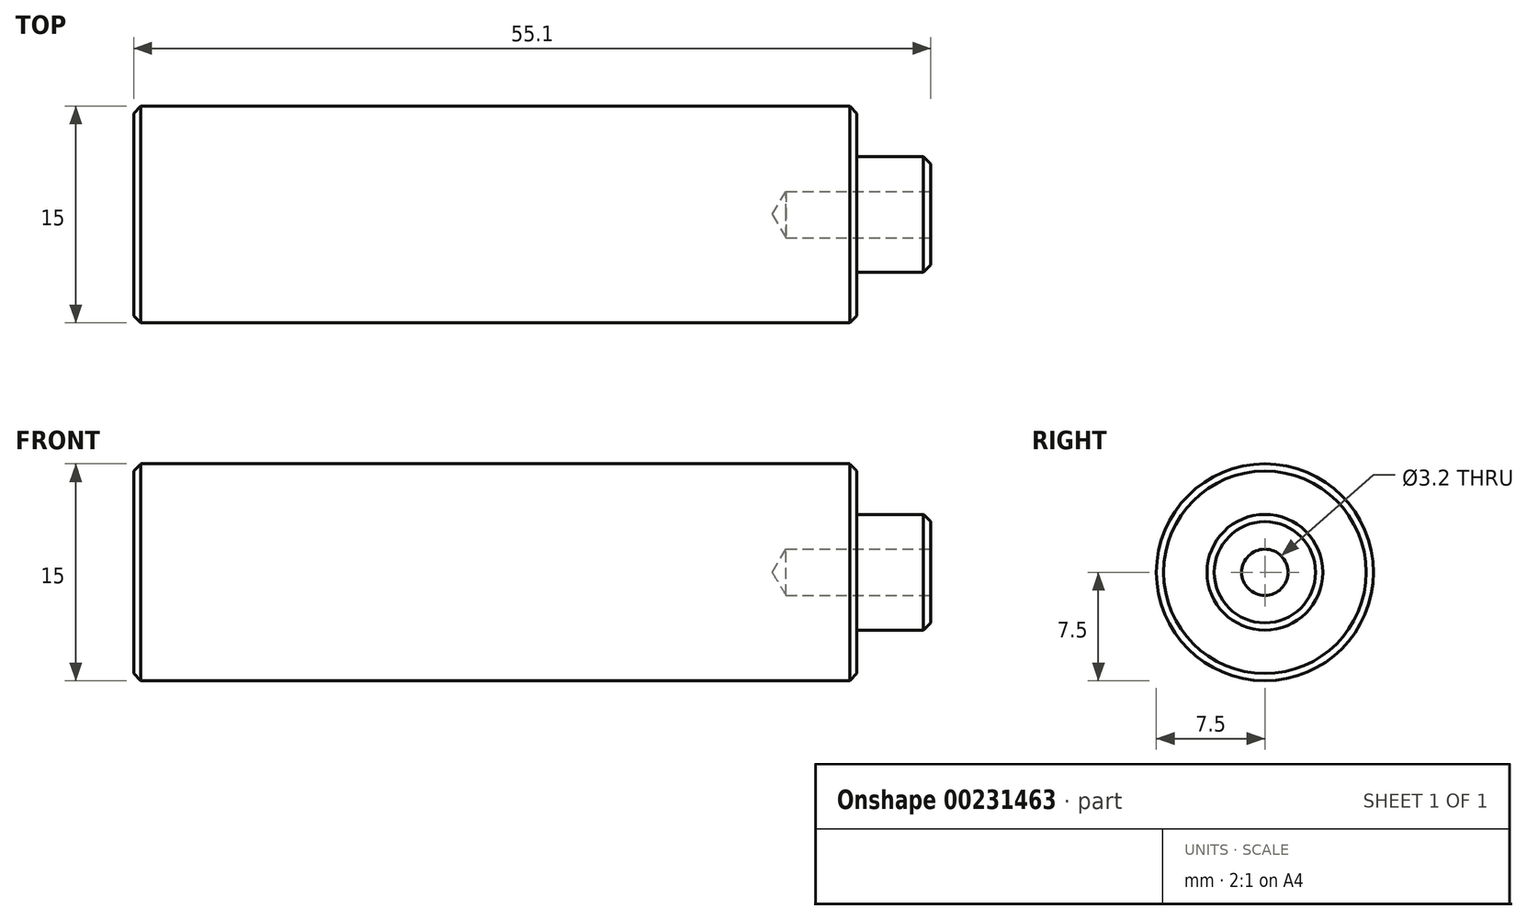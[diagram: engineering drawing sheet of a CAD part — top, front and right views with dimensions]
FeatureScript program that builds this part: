
annotation { "Feature Type Name" : "Feature", "Feature Type Description" : "" }
export const myFeature = defineFeature(function(context is Context, id is Id, definition is map)
    precondition{}
    {
        {
            var Q0;
            Q0=qCreatedBy(makeId("Front.planeOp"),FACE);
            var sketch = newSketch(context, id + "F0", { "sketchPlane" : qUnion([Q0])});
            skLineSegment(sketch, "E0.bottom", {"start": v(0, 0) * mm, "end": v(50, 0) * mm});
            skLineSegment(sketch, "E0.top", {"start": v(0, 7.5) * mm, "end": v(50, 7.5) * mm});
            skLineSegment(sketch, "E0.left", {"start": v(0, 0) * mm, "end": v(0, 7.5) * mm});
            skLineSegment(sketch, "E0.right", {"start": v(50, 4) * mm, "end": v(50, 7.5) * mm});
            skLineSegment(sketch, "E1.bottom", {"start": v(50, 0) * mm, "end": v(55.1, 0) * mm});
            skLineSegment(sketch, "E1.top", {"start": v(50, 4) * mm, "end": v(55.1, 4) * mm});
            skLineSegment(sketch, "E1.right", {"start": v(55.1, 0) * mm, "end": v(55.1, 4) * mm});
            skSolve(sketch);
        }
        {
            var Q0;
            Q0=makeQuery(id+"F0.imprint","IMPRINT",FACE,{"disambiguationData":[TD([[makeQuery(id+"F0.imprint","IMPRINT",EDGE,{"derivedFrom":sQuery(id+"F0.wireOp",EDGE,"E0.bottom")}),1.0]])]});
            var Q1;
            Q1=sQuery(id+"F0.wireOp",EDGE,"E0.bottom");
            revolve(context, id + "F1", {"entities" : qUnion([Q0]), "axis" : qUnion([Q1]), "revolveType" : RevolveType.FULL});
        }
        {
            var Q0;
            Q0=makeQuery(id+"F1.opRevolve","SWEPT_FACE",FACE,{"disambiguationData":[OSD([sQuery(id+"F0.wireOp",EDGE,"E1.right")])]});
            var sketch = newSketch(context, id + "F2", { "sketchPlane" : qUnion([Q0])});
            skPoint(sketch, "E2", {"position": v(0, 0) * mm});
            skSolve(sketch);
        }
        {
            var Q0;
            Q0=sQuery(id+"F2.wireOp",VERTEX,"E2");
            var Q1;
            Q1=makeQuery(id+"F1.opRevolve","SWEPT_BODY",BODY,{"disambiguationData":[OSD([sQuery(id+"F0.wireOp",EDGE,"E0.bottom"),sQuery(id+"F0.wireOp",EDGE,"E0.top"),sQuery(id+"F0.wireOp",EDGE,"E0.left"),sQuery(id+"F0.wireOp",EDGE,"E0.right"),sQuery(id+"F0.wireOp",EDGE,"E1.bottom"),sQuery(id+"F0.wireOp",EDGE,"E1.top"),sQuery(id+"F0.wireOp",EDGE,"E1.right")])]});
            hole(context, id + "F3", {"style" : HoleStyle.SIMPLE, "endStyle" : HoleEndStyle.BLIND, "standardTappedOrClearance" : lookupTablePath({ "standard" : "ISO", "engagement" : "75%", "pitch" : "0.75 mm", "size" : "M4", "type" : "Tapped" }), "standardBlindInLast" : lookupTablePath({ "standard" : "ISO", "engagement" : "75%", "pitch" : "0.75 mm", "size" : "M4", "type" : "Tapped" }), "holeDiameter" : 3.2 * mm, "holeDepth" : 10 * mm, "startFromSketch" : true, "locations" : qUnion([Q0]), "scope" : qUnion([Q1])});
        }
        {
            var Q0;
            Q0=makeQuery(id+"F1.opRevolve","SWEPT_FACE",FACE,{"disambiguationData":[OSD([sQuery(id+"F0.wireOp",EDGE,"E0.top")])]});
            var Q1;
            Q1=makeQuery(id+"F1.opRevolve","SWEPT_EDGE",EDGE,{"disambiguationData":[OSD([sQuery(id+"F0.wireOp",EDGE,"E1.top"),sQuery(id+"F0.wireOp",EDGE,"E1.right")])]});
            var Q2;
            Q2=makeQuery(id+"F3.hole-0.boolean.opBoolean","COPY",EDGE,{"derivedFrom":makeQuery(id+"F3.hole-0.opRevolve","SWEPT_EDGE",EDGE,{"disambiguationData":[OSD([sQuery(id+"F3.hole-0.sketch.wireOp",EDGE,"core_line_2"),sQuery(id+"F3.hole-0.sketch.wireOp",EDGE,"core_line_3")])]})});
            chamfer(context, id + "F4", {"entities" : qUnion([Q0, Q1, Q2]), "width" : 0.5 * mm, "tangentPropagation" : true});
        }
    });
